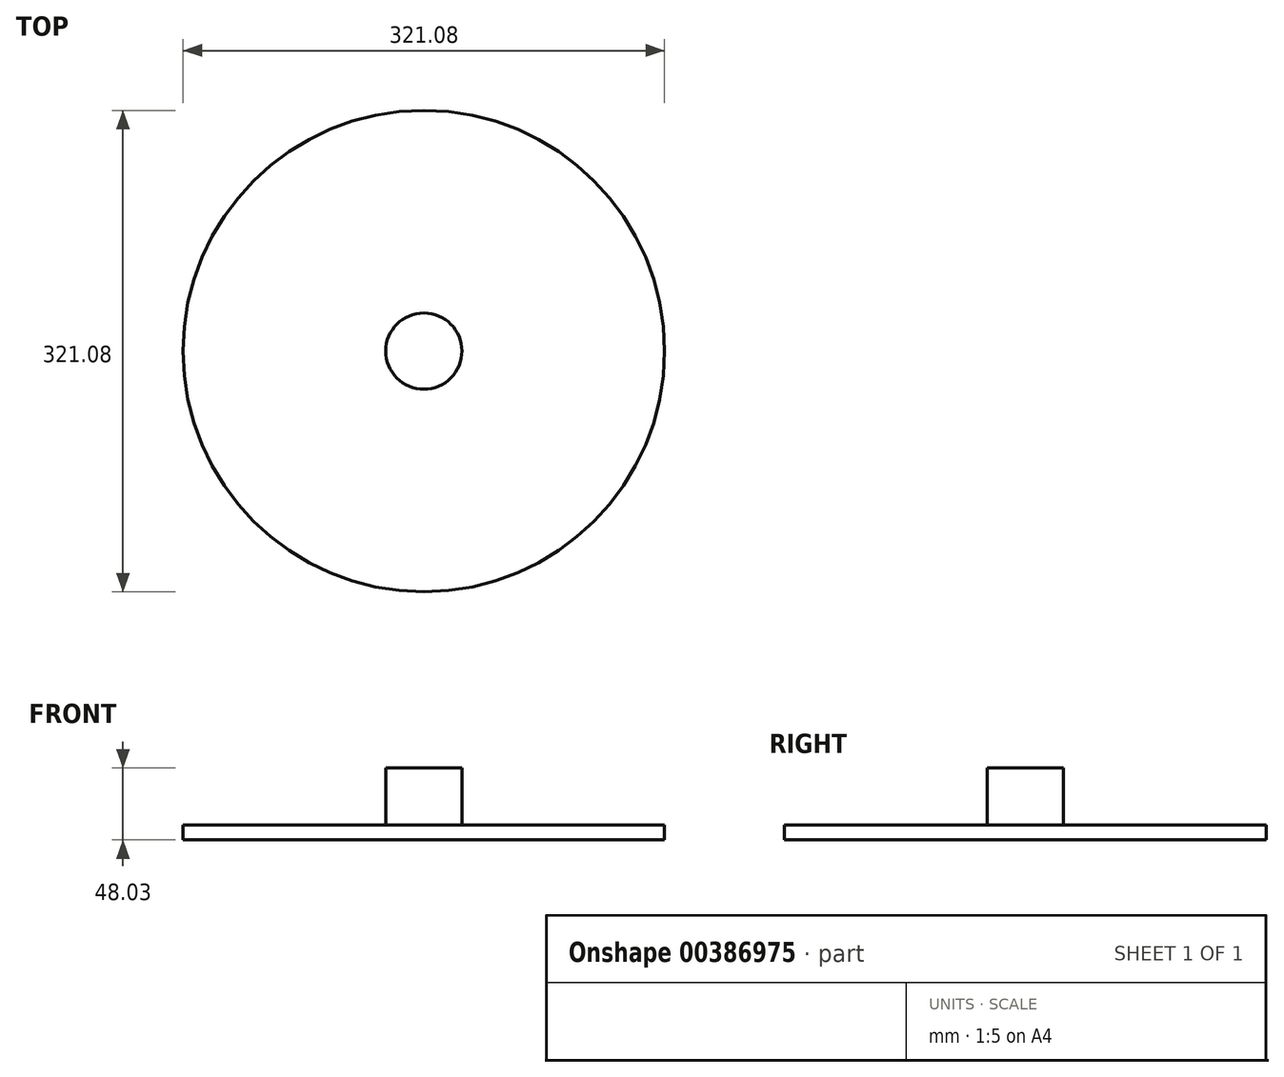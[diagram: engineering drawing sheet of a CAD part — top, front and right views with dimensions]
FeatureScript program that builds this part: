
annotation { "Feature Type Name" : "Feature", "Feature Type Description" : "" }
export const myFeature = defineFeature(function(context is Context, id is Id, definition is map)
    precondition{}
    {
        {
            var Q0;
            Q0=qCreatedBy(makeId("Right.planeOp"),FACE);
            var sketch = newSketch(context, id + "F0", { "sketchPlane" : qUnion([Q0])});
            skLineSegment(sketch, "E0.bottom", {"start": v(-143.21, -42.25) * mm, "end": v(-105.7, -42.25) * mm});
            skLineSegment(sketch, "E0.top", {"start": v(-143.21, -32.32) * mm, "end": v(-8.07, -32.32) * mm});
            skLineSegment(sketch, "E0.left", {"start": v(-143.21, -42.25) * mm, "end": v(-143.21, -32.32) * mm});
            skLineSegment(sketch, "E1", {"start": v(-8.07, -32.32) * mm, "end": v(-8.07, 5.78) * mm});
            skLineSegment(sketch, "E2", {"start": v(-8.07, 5.78) * mm, "end": v(17.33, 5.78) * mm});
            skLineSegment(sketch, "E3", {"start": v(17.33, 5.78) * mm, "end": v(17.33, -42.25) * mm});
            skLineSegment(sketch, "E4", {"start": v(17.33, -42.25) * mm, "end": v(-105.7, -42.25) * mm});
            skSolve(sketch);
        }
        {
            var Q0;
            Q0=makeQuery(id+"F0.imprint","IMPRINT",FACE,{"disambiguationData":[TD([[makeQuery(id+"F0.imprint","IMPRINT",EDGE,{"derivedFrom":sQuery(id+"F0.wireOp",EDGE,"E0.bottom")}),1.0]])]});
            var Q1;
            Q1=sQuery(id+"F0.wireOp",EDGE,"E3");
            revolve(context, id + "F1", {"entities" : qUnion([Q0]), "axis" : qUnion([Q1]), "revolveType" : RevolveType.FULL});
        }
    });
